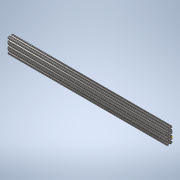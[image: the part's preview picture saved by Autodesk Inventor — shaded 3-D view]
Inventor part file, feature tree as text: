
AUTODESK INVENTOR PART (.ipt)
format: ipt  version: 2020 (Build 240168000, 168)  size: 393,728 bytes
history: native  units: in
note: dims shown in document units (in); Inventor stores cm internally (conversion verified against a paired STEP export)
features: sketch x2, extrude x1
ambient origin geometry x8: Origin, YZ Plane, XZ Plane, XY Plane, X Axis, Y Axis, Z Axis, Center Point
bodies: Solid1 (feature_tree)
feature tree (3):
  extrude  "Extrusion1"  [1 undecoded]
  sketch  "Sketch2"
  sketch  "Sketch1"  dims[d0=31.0in d1=0.0in]
note: 1 required parameter value undecoded (feature->parameter linkage not recoverable at this tier; creation-order binding heuristic only, values carry confidence <= 0.55)
